# Revit family: Dune 3-641-xxxx
name_source: partatom
category: Generic Models
units: mm (PartAtom-declared; Revit-internal decimal feet)

## family parameters
Always vertical = Yes
Can host rebar = No
Cut with Voids When Loaded = No
Host = Ceiling
Part Type = Normal
Room Calculation Point = No
Round Connector Dimension = Use Diameter
Shared = No

## types (4) — shared parameters
Manufacturer = Oxygen - Lighting & Fans
Model = 3-641-xxxx / Dune Pendant
References = Ref. 3 = 120 V / Ref. 37 = 277 V
URL = www.oxygenlighting.com
Voltage Input = 120 V or 277 V - 50/60 Hz
zero-valued in all types: Default Elevation

## per-type parameters (varying)
| type | Metal finish | Shell Finish | Voltage |
| 3-641-1624 / Gray - Satin Nickel | 16 - Gray | 24 - Satin Nickel | 120 V |
| 3-641-1540d / Black - Aged Brass | 15 - Black | 40 - Aged Brass | 120 V |
| 37-641-1540d / Black - Aged Brass | 15 - Black | 40 - Aged Brass | 277 V |
| 37-641-1624 / Gray - Satin Nickel | 16 - Gray | 24 - Satin Nickel | 277 V |

## geometry (parser evidence)
native form markers: Sweep x5
no freeform markers — native parametric forms only
